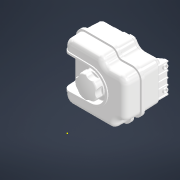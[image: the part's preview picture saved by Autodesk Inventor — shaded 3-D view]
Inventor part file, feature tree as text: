
AUTODESK INVENTOR PART (.ipt)
format: ipt  version: 2022 (Build 260153000, 153)  size: 4,744,704 bytes
history: native  units: in
note: dims shown in document units (in); Inventor stores cm internally (conversion verified against a paired STEP export)
features: other x2, sketch x1
ambient origin geometry x8: Origin, YZ Plane, XZ Plane, XY Plane, X Axis, Y Axis, Z Axis, Center Point
bodies: Body1 (feature_tree)
feature tree (3):
  other  "Sólido1"
  sketch  "Esboço1"
  other  "Boss-Extrude11"
